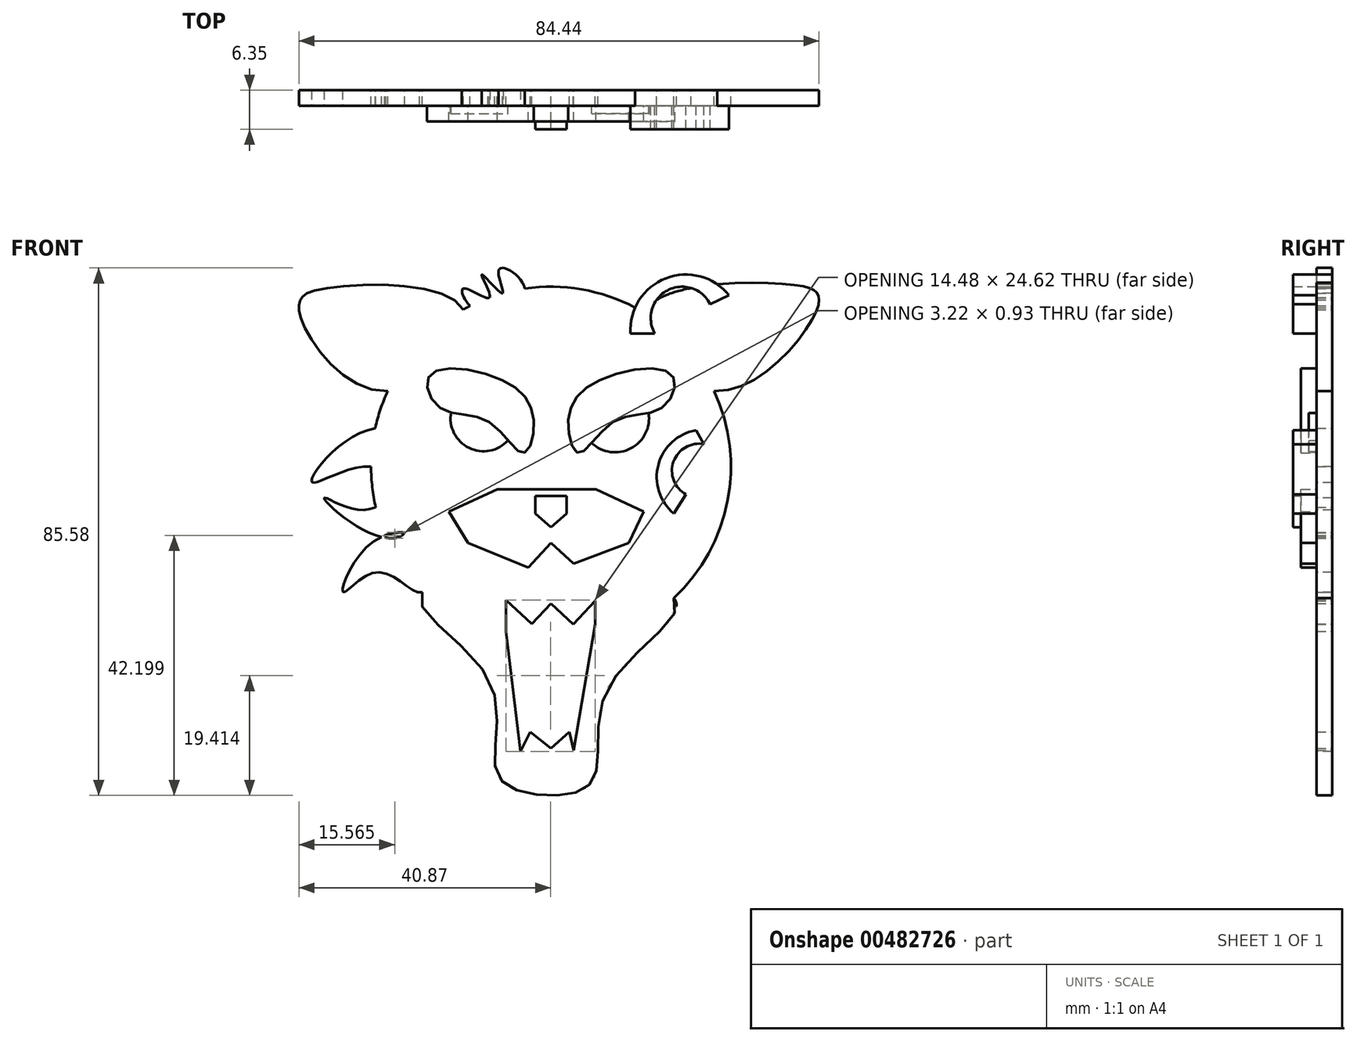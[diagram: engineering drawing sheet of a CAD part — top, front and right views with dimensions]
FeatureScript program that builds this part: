
annotation { "Feature Type Name" : "Feature", "Feature Type Description" : "" }
export const myFeature = defineFeature(function(context is Context, id is Id, definition is map)
    precondition{}
    {
        {
            var Q0;
            Q0=qCreatedBy(makeId("Front.planeOp"),FACE);
            var sketch = newSketch(context, id + "F0", { "sketchPlane" : qUnion([Q0])});
            skCircle(sketch, "E0", {"center": v(0, 0) * mm, "radius": 29.2 * mm});
            skFitSpline(sketch, "E1", {"points": [v(-20.92, -20.37) * mm, v(-10.1, -34.53) * mm, v(-8.7, -49.97) * mm, v(0, -53.34) * mm, v(7.02, -50.53) * mm, v(9.55, -35.37) * mm, v(19.93, -21.34) * mm, v(-20.92, -20.37) * mm]});
            skFitSpline(sketch, "E2", {"points": [v(-26.5, 12.27) * mm, v(-40.43, 23.58) * mm, v(-40.7, 26.95) * mm, v(-38.18, 28.64) * mm, v(-14.22, 25.5) * mm, v(-26.5, 12.27) * mm]});
            skFitSpline(sketch, "E3", {"points": [v(26.5, 12.27) * mm, v(42.95, 24.99) * mm, v(43.23, 28.07) * mm, v(39.58, 29.48) * mm, v(15.1, 25) * mm, v(26.5, 12.27) * mm]});
            skFitSpline(sketch, "E4", {"points": [v(-20.92, -20.37) * mm, v(-28.07, -17.12) * mm, v(-33.69, -20.37) * mm, v(-29.76, -12.91) * mm, v(-20.92, -12.35) * mm, v(-20.92, -20.37) * mm]});
            skFitSpline(sketch, "E5", {"points": [v(-23.75, -10.72) * mm, v(-31.72, -9.55) * mm, v(-36.78, -5.05) * mm, v(-30.6, -7.02) * mm, v(-24.14, -5.61) * mm, v(-23.75, -10.72) * mm]});
            skFitSpline(sketch, "E6", {"points": [v(-20.92, -3.09) * mm, v(-29.2, 0) * mm, v(-38.74, -2.53) * mm, v(-32.28, 4.77) * mm, v(-20.92, 4.21) * mm, v(-20.92, -3.09) * mm]});
            skFitSpline(sketch, "E7", {"points": [v(-10.67, 24.42) * mm, v(-14.22, 28.92) * mm, v(-9.96, 27.45) * mm, v(-11.23, 31.16) * mm, v(-7.86, 28.12) * mm, v(-8.42, 32) * mm, v(-4.24, 28.89) * mm, v(-10.67, 24.42) * mm]});
            skSolve(sketch);
        }
        {
            var Q0;
            Q0=qSketchRegion(id+"F0",true);
            extrude(context, id + "F1", {"entities" : qUnion([Q0]), "depth" : 2.54 * mm});
        }
        {
            var Q0;
            Q0=qCreatedBy(makeId("Front.planeOp"),FACE);
            var sketch = newSketch(context, id + "F2", { "sketchPlane" : qUnion([Q0])});
            skFitSpline(sketch, "E8", {"points": [v(-17.97, 9.55) * mm, v(-10.1, 7.3) * mm, v(-4.5, 2.25) * mm, v(-2.8, 7.58) * mm, v(-7.86, 14.04) * mm, v(-19.65, 14.88) * mm, v(-17.97, 9.55) * mm]});
            skLineSegment(sketch, "E9", {"start": v(-8.7, -3.65) * mm, "end": v(0, -3.65) * mm});
            skLineSegment(sketch, "E10", {"start": v(0, -3.65) * mm, "end": v(7.3, -3.65) * mm});
            skLineSegment(sketch, "E11", {"start": v(7.3, -3.65) * mm, "end": v(15.02, -7.3) * mm});
            skLineSegment(sketch, "E12", {"start": v(15.02, -7.3) * mm, "end": v(12.63, -12.35) * mm});
            skLineSegment(sketch, "E13", {"start": v(12.63, -12.35) * mm, "end": v(3.65, -15.72) * mm});
            skLineSegment(sketch, "E14", {"start": v(3.65, -15.72) * mm, "end": v(0, -12.35) * mm});
            skLineSegment(sketch, "E15", {"start": v(0, -12.35) * mm, "end": v(-3.68, -16.34) * mm});
            skLineSegment(sketch, "E16", {"start": v(-3.68, -16.34) * mm, "end": v(-13.48, -12.35) * mm});
            skLineSegment(sketch, "E17", {"start": v(-13.48, -12.35) * mm, "end": v(-16.56, -7.3) * mm});
            skLineSegment(sketch, "E18", {"start": v(-16.56, -7.3) * mm, "end": v(-8.7, -3.65) * mm});
            skFitSpline(sketch, "E19.MirrorC", {"points": [v(17.97, 9.55) * mm, v(10.1, 7.3) * mm, v(4.5, 2.25) * mm, v(2.8, 7.58) * mm, v(7.86, 14.04) * mm, v(19.65, 14.88) * mm, v(17.97, 9.55) * mm]});
            skSolve(sketch);
        }
        {
            var Q0;
            Q0=qSketchRegion(id+"F2",true);
            extrude(context, id + "F3", {"entities" : qUnion([Q0]), "operationType" : NewBodyOperationType.ADD, "depth" : 5.08 * mm});
        }
        {
            var Q0;
            Q0=qCreatedBy(makeId("Front.planeOp"),FACE);
            var sketch = newSketch(context, id + "F4", { "sketchPlane" : qUnion([Q0])});
            skLineSegment(sketch, "E20", {"start": v(-7.3, -26.7) * mm, "end": v(-7.3, -21.62) * mm});
            skLineSegment(sketch, "E21", {"start": v(-7.3, -21.62) * mm, "end": v(-3.09, -25.55) * mm});
            skLineSegment(sketch, "E22", {"start": v(-3.09, -25.55) * mm, "end": v(0, -22.24) * mm});
            skLineSegment(sketch, "E23", {"start": v(0, -22.24) * mm, "end": v(3.6, -25.6) * mm});
            skLineSegment(sketch, "E24", {"start": v(3.6, -25.6) * mm, "end": v(7.18, -21.77) * mm});
            skLineSegment(sketch, "E25", {"start": v(7.18, -21.77) * mm, "end": v(7.18, -25.6) * mm});
            skLineSegment(sketch, "E26", {"start": v(7.18, -25.6) * mm, "end": v(3.6, -46.6) * mm});
            skLineSegment(sketch, "E27", {"start": v(-4.93, -46.6) * mm, "end": v(-7.3, -26.7) * mm});
            skLineSegment(sketch, "E28", {"start": v(3.6, -46.6) * mm, "end": v(-4.93, -46.6) * mm});
            skSolve(sketch);
        }
        {
            var Q0;
            Q0=qSketchRegion(id+"F4",true);
            extrude(context, id + "F5", {"entities" : qUnion([Q0]), "operationType" : NewBodyOperationType.REMOVE, "oppositeDirection" : true, "depth" : -2.54 * mm});
        }
        {
            var Q0;
            Q0=qCreatedBy(makeId("Front.planeOp"),FACE);
            var sketch = newSketch(context, id + "F6", { "sketchPlane" : qUnion([Q0])});
            skCircle(sketch, "E29", {"center": v(-10.95, 7.86) * mm, "radius": 5.36 * mm});
            skCircle(sketch, "E30", {"center": v(10.39, 7.86) * mm, "radius": 5.53 * mm});
            skSolve(sketch);
        }
        {
            var Q0;
            Q0=qSketchRegion(id+"F6",true);
            extrude(context, id + "F7", {"entities" : qUnion([Q0]), "operationType" : NewBodyOperationType.ADD, "depth" : 3.8 * mm});
        }
        {
            var Q0;
            Q0=qCreatedBy(makeId("Front.planeOp"),FACE);
            var sketch = newSketch(context, id + "F8", { "sketchPlane" : qUnion([Q0])});
            skLineSegment(sketch, "E31", {"start": v(0, -9.83) * mm, "end": v(-2.53, -7.58) * mm});
            skLineSegment(sketch, "E32", {"start": v(-2.53, -7.58) * mm, "end": v(-2.53, -4.77) * mm});
            skLineSegment(sketch, "E33", {"start": v(-2.53, -4.77) * mm, "end": v(2.53, -4.77) * mm});
            skLineSegment(sketch, "E34", {"start": v(2.53, -4.77) * mm, "end": v(2.53, -7.58) * mm});
            skLineSegment(sketch, "E35", {"start": v(2.53, -7.58) * mm, "end": v(0, -9.83) * mm});
            skSolve(sketch);
        }
        {
            var Q0;
            Q0=qSketchRegion(id+"F8",true);
            extrude(context, id + "F9", {"entities" : qUnion([Q0]), "operationType" : NewBodyOperationType.ADD, "depth" : 6.35 * mm});
        }
        {
            var Q0;
            Q0=qCreatedBy(makeId("Front.planeOp"),FACE);
            var sketch = newSketch(context, id + "F10", { "sketchPlane" : qUnion([Q0])});
            skArc(sketch, "E36", {"start": v(23.58, 5.9) * mm, "mid": v(17.43, 0.33) * mm, "end": v(19.93, -7.58) * mm});
            skArc(sketch, "E37", {"start": v(24.83, 3.65) * mm, "mid": v(19.9, 0.83) * mm, "end": v(21.9, -4.5) * mm});
            skArc(sketch, "E38", {"start": v(28.92, 27.8) * mm, "mid": v(18.65, 30.58) * mm, "end": v(12.91, 21.62) * mm});
            skArc(sketch, "E39", {"start": v(25.83, 26.39) * mm, "mid": v(18.9, 28.6) * mm, "end": v(16.84, 21.62) * mm});
            skLineSegment(sketch, "E40", {"start": v(12.91, 21.62) * mm, "end": v(16.84, 21.62) * mm});
            skLineSegment(sketch, "E41", {"start": v(25.83, 26.39) * mm, "end": v(28.92, 27.8) * mm});
            skLineSegment(sketch, "E42", {"start": v(24.83, 3.65) * mm, "end": v(23.58, 5.9) * mm});
            skLineSegment(sketch, "E43", {"start": v(19.93, -7.58) * mm, "end": v(21.9, -4.5) * mm});
            skSolve(sketch);
        }
        {
            var Q0;
            Q0=qSketchRegion(id+"F10",true);
            extrude(context, id + "F11", {"entities" : qUnion([Q0]), "operationType" : NewBodyOperationType.ADD, "depth" : 6.35 * mm});
        }
        {
            var Q0;
            Q0=qCreatedBy(makeId("Front.planeOp"),FACE);
            var sketch = newSketch(context, id + "F12", { "sketchPlane" : qUnion([Q0])});
            skLineSegment(sketch, "E44", {"start": v(4.07, -47.62) * mm, "end": v(2.99, -43.03) * mm});
            skLineSegment(sketch, "E45", {"start": v(2.99, -43.03) * mm, "end": v(0, -45.73) * mm});
            skLineSegment(sketch, "E46", {"start": v(-3.4, -43.06) * mm, "end": v(-5.84, -47.96) * mm});
            skLineSegment(sketch, "E47", {"start": v(-5.84, -47.96) * mm, "end": v(4.07, -47.62) * mm});
            skLineSegment(sketch, "E48", {"start": v(0, -45.73) * mm, "end": v(-3.4, -43.06) * mm});
            skSolve(sketch);
        }
        {
            var Q0;
            Q0=qSketchRegion(id+"F12",true);
            extrude(context, id + "F13", {"entities" : qUnion([Q0]), "operationType" : NewBodyOperationType.ADD, "depth" : 2.54 * mm});
        }
    });
